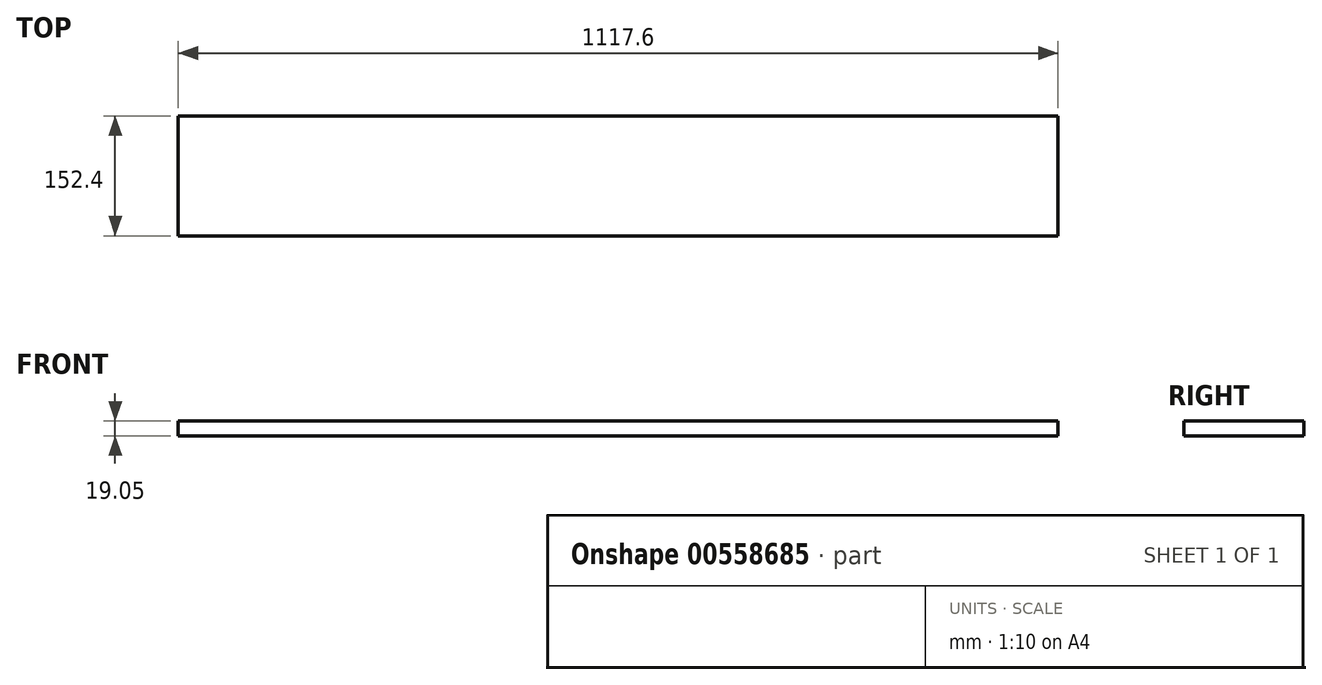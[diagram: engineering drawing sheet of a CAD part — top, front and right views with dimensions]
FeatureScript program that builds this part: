
annotation { "Feature Type Name" : "Feature", "Feature Type Description" : "" }
export const myFeature = defineFeature(function(context is Context, id is Id, definition is map)
    precondition{}
    {
        {
            var Q0;
            Q0=qCreatedBy(makeId("Top.planeOp"),FACE);
            var sketch = newSketch(context, id + "F0", { "sketchPlane" : qUnion([Q0])});
            skLineSegment(sketch, "E0.bottom", {"start": v(-304.73, 27.1) * mm, "end": v(812.87, 27.1) * mm});
            skLineSegment(sketch, "E0.top", {"start": v(-304.73, -125.3) * mm, "end": v(812.87, -125.3) * mm});
            skLineSegment(sketch, "E0.left", {"start": v(-304.73, 27.1) * mm, "end": v(-304.73, -125.3) * mm});
            skLineSegment(sketch, "E0.right", {"start": v(812.87, 27.1) * mm, "end": v(812.87, -125.3) * mm});
            skSolve(sketch);
        }
        {
            var Q0;
            Q0 = qSketchRegion(id + "F0", true);
            extrude(context, id + "F1", {"entities" : qUnion([Q0]), "depth" : 19.05 * mm, "offsetDistance" : 25.4 * mm});
        }
    });
